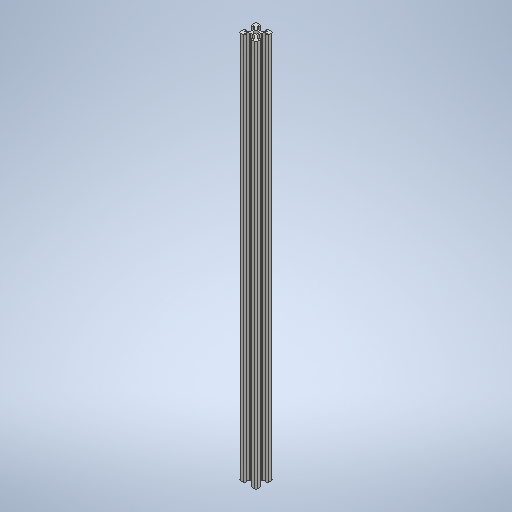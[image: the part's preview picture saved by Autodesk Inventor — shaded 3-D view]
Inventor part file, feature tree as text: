
AUTODESK INVENTOR PART (.ipt)
format: ipt  version: 2025.2 (Build 292293000, 293)  size: 404,480 bytes
history: native  units: mm
features: other x1, extrude x1, sketch x1
ambient origin geometry x8: Origin, YZ Plane, XZ Plane, XY Plane, X Axis, Y Axis, Z Axis, Center Point
bodies: Body1 (feature_tree)
feature tree (3):
  other  "Твердое тело1"
  extrude  "Выдавливание1"  Depth=0.25mm
  sketch  "Эскиз1"
